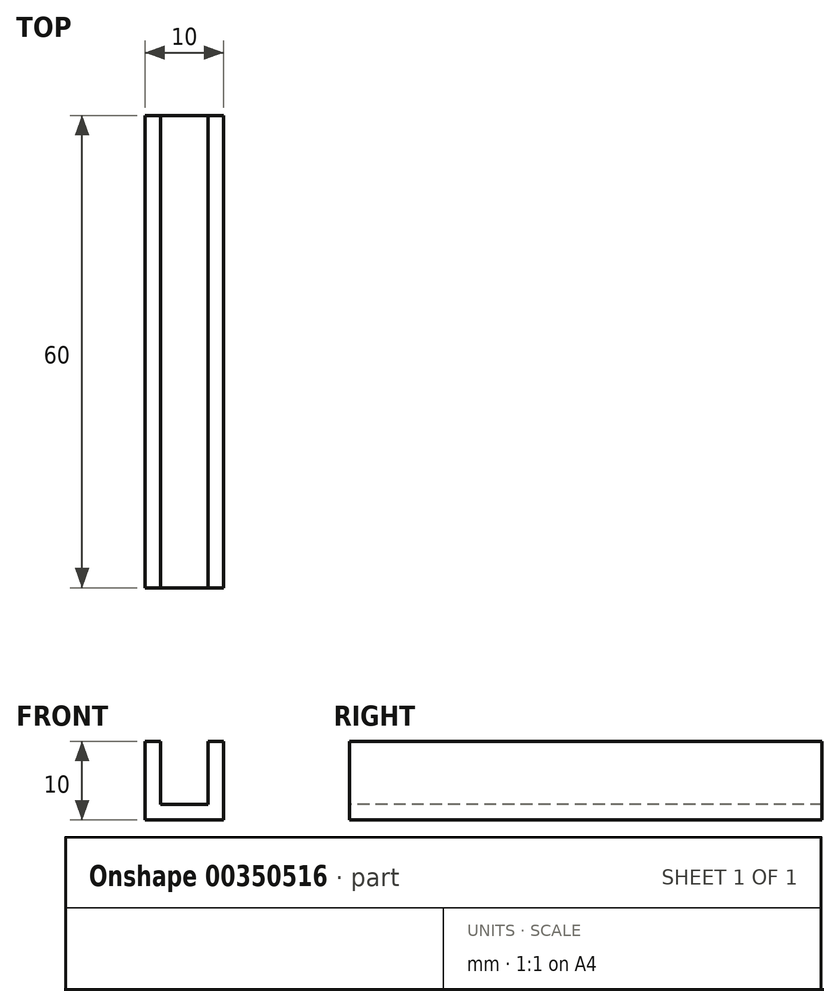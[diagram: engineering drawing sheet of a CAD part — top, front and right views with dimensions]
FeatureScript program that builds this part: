
annotation { "Feature Type Name" : "Feature", "Feature Type Description" : "" }
export const myFeature = defineFeature(function(context is Context, id is Id, definition is map)
    precondition{}
    {
        {
            var Q0;
            Q0=qCreatedBy(makeId("Top.planeOp"),FACE);
            var sketch = newSketch(context, id + "F0", { "sketchPlane" : qUnion([Q0])});
            skLineSegment(sketch, "E0.bottom", {"start": v(-5, 5) * mm, "end": v(5, 5) * mm});
            skLineSegment(sketch, "E0.top", {"start": v(-5, -5) * mm, "end": v(5, -5) * mm});
            skLineSegment(sketch, "E0.left", {"start": v(-5, 5) * mm, "end": v(-5, -5) * mm});
            skLineSegment(sketch, "E0.right", {"start": v(5, 5) * mm, "end": v(5, -5) * mm});
            skPoint(sketch, "E0.middle", {"position": v(0, 0) * mm});
            skSolve(sketch);
        }
        {
            var Q0;
            Q0=makeQuery(id+"F0.imprint","IMPRINT",FACE,{"disambiguationData":[TD([[makeQuery(id+"F0.imprint","IMPRINT",EDGE,{"derivedFrom":sQuery(id+"F0.wireOp",EDGE,"E0.bottom")}),-1.0]])]});
            extrude(context, id + "F1", {"entities" : qUnion([Q0]), "depth" : 2 * mm});
        }
        {
            var Q0;
            Q0=makeQuery(id+"F1.opExtrude","CAP_FACE",FACE,{"disambiguationData":[OSD([sQuery(id+"F0.wireOp",EDGE,"E0.bottom"),sQuery(id+"F0.wireOp",EDGE,"E0.top"),sQuery(id+"F0.wireOp",EDGE,"E0.left"),sQuery(id+"F0.wireOp",EDGE,"E0.right")])],"isStart":false});
            var sketch = newSketch(context, id + "F2", { "sketchPlane" : qUnion([Q0])});
            skLineSegment(sketch, "E1.bottom", {"start": v(-5, 5) * mm, "end": v(-3, 5) * mm});
            skLineSegment(sketch, "E1.top", {"start": v(-5, -5) * mm, "end": v(-3, -5) * mm});
            skLineSegment(sketch, "E1.left", {"start": v(-5, 5) * mm, "end": v(-5, -5) * mm});
            skLineSegment(sketch, "E1.right", {"start": v(-3, 5) * mm, "end": v(-3, -5) * mm});
            skLineSegment(sketch, "E2.bottom", {"start": v(5, 5) * mm, "end": v(3, 5) * mm});
            skLineSegment(sketch, "E2.top", {"start": v(5, -5) * mm, "end": v(3, -5) * mm});
            skLineSegment(sketch, "E2.left", {"start": v(5, 5) * mm, "end": v(5, -5) * mm});
            skLineSegment(sketch, "E2.right", {"start": v(3, 5) * mm, "end": v(3, -5) * mm});
            skSolve(sketch);
        }
        {
            var Q0;
            Q0=makeQuery(id+"F2.imprint","IMPRINT",FACE,{"disambiguationData":[TD([[makeQuery(id+"F2.imprint","IMPRINT",EDGE,{"derivedFrom":sQuery(id+"F2.wireOp",EDGE,"E1.bottom")}),-1.0]])]});
            var Q1;
            Q1=makeQuery(id+"F2.imprint","IMPRINT",FACE,{"disambiguationData":[TD([[makeQuery(id+"F2.imprint","IMPRINT",EDGE,{"derivedFrom":sQuery(id+"F2.wireOp",EDGE,"E2.bottom")}),-1.0]])]});
            extrude(context, id + "F3", {"entities" : qUnion([Q0, Q1]), "operationType" : NewBodyOperationType.ADD, "depth" : 8 * mm});
        }
        {
            var Q0;
            Q0=makeQuery(id+"F3.boolean.opBoolean","MERGE",FACE,{"derivedFrom":[makeQuery(id+"F1.opExtrude","SWEPT_FACE",FACE,{"disambiguationData":[OSD([sQuery(id+"F0.wireOp",EDGE,"E0.bottom")])]}),makeQuery(id+"F3.opExtrude","SWEPT_FACE",FACE,{"disambiguationData":[OSD([sQuery(id+"F2.wireOp",EDGE,"E1.bottom")])]}),makeQuery(id+"F3.opExtrude","SWEPT_FACE",FACE,{"disambiguationData":[OSD([sQuery(id+"F2.wireOp",EDGE,"E2.bottom")])]})]});
            var sketch = newSketch(context, id + "F4", { "sketchPlane" : qUnion([Q0])});
            skSolve(sketch);
        }
        {
            var Q0;
            Q0 = qSketchRegion(id + "F4", true);
            var Q1;
            {var subQ2=sQuery(id+"F0.wireOp",EDGE,"E0.bottom");Q1=makeQuery(id+"F4.imprint","IMPRINT",FACE,{"disambiguationData":[TD([[makeQuery(id+"F4.imprint","IMPRINT",EDGE,{"derivedFrom":makeQuery(id+"F1.opExtrude","CAP_EDGE",EDGE,{"disambiguationData":[OSD([subQ2])],"isStart":true})}),-1.0]])]});}
            extrude(context, id + "F5", {"entities" : qUnion([Q0, Q1]), "operationType" : NewBodyOperationType.ADD, "depth" : 50 * mm});
        }
    });
